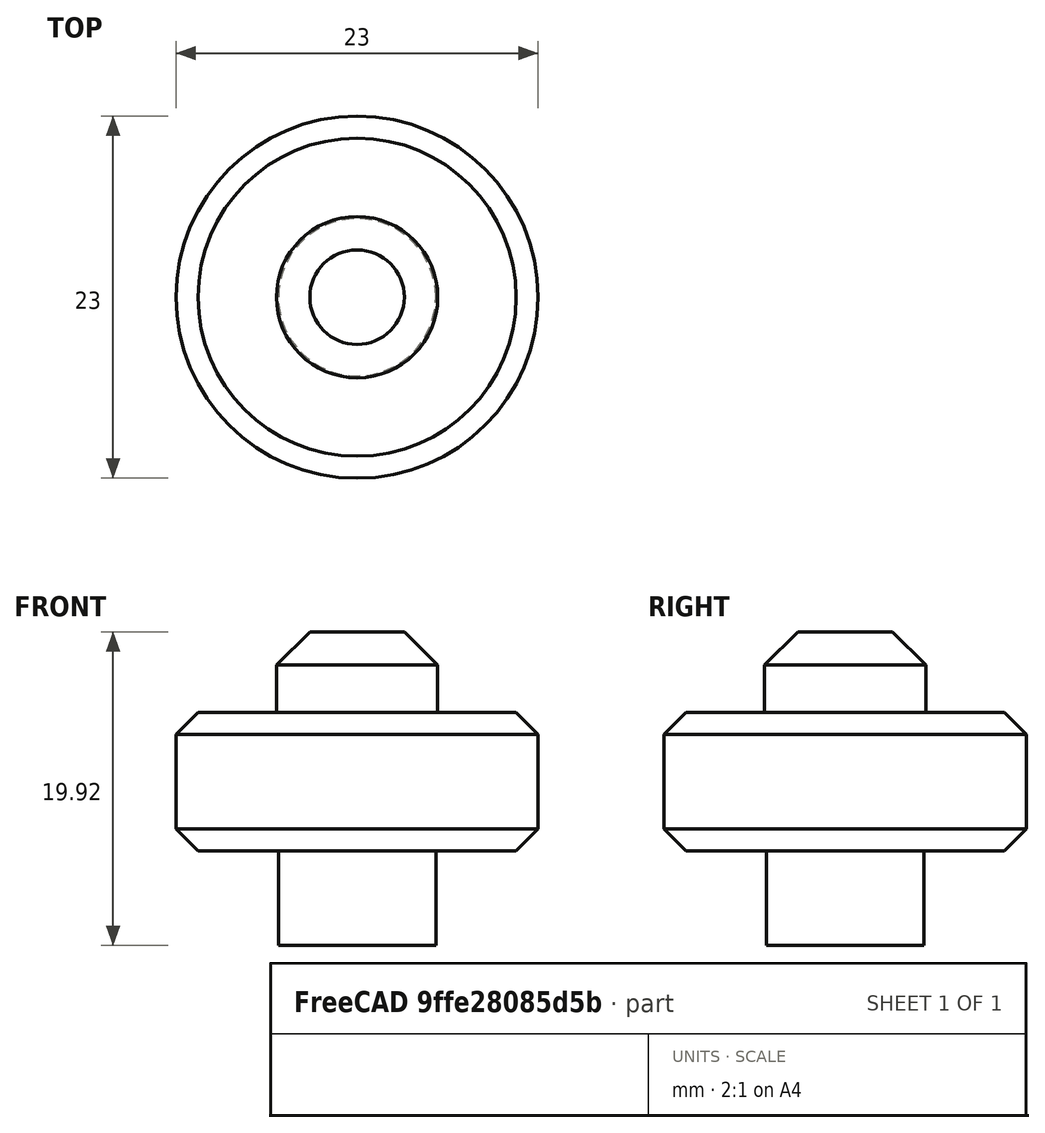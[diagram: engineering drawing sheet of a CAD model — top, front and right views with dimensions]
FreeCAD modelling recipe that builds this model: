
FCSTD DOCUMENT  (FreeCAD 0.20R29177 +426 (Git))
Label: GantryWheel
License: All rights reserved
LicenseURL: http://en.wikipedia.org/wiki/All_rights_reserved
objects: App::DocumentObjectGroup×3, PartDesign::CoordinateSystem×1, App::FeaturePython×1, Sketcher::SketchObject×1, PartDesign::Revolution×1, PartDesign::Body×1, App::Part×1
note: 5 computed .brp shape members not serialized (recipe doc carries the construction recipe); baked Part::Feature solids carry a one-line shape summary decoded from their .brp

FEATURE [App::DocumentObjectGroup] Parts
FEATURE [PartDesign::CoordinateSystem] LCS_Origin
  AttacherType = Attacher::AttachEngine3D
  MapMode = 2
  Support = -> [X_Axis]
FEATURE [App::FeaturePython] Variables  # WARN: FeaturePython — macro-defined, semantics opaque (R4)
  Type = App::PropertyContainer
FEATURE [App::DocumentObjectGroup] Constraints
FEATURE [App::DocumentObjectGroup] Configurations
FEATURE [Sketcher::SketchObject] Sketch
  FullyConstrained = true
  MapMode = 5
  Placement = pos=(0,0,0) rot=(1,0,0;1.5708rad)
  Support = -> [XZ_Plane001]
  sketch-geometry (11):
    g0: LineSegment StartX=0 StartY=19.9213 StartZ=0 EndX=3 EndY=19.9213 EndZ=0
    g1: LineSegment StartX=3 StartY=19.9213 StartZ=0 EndX=5.12132 EndY=17.8 EndZ=0
    g2: LineSegment StartX=5.12132 StartY=17.8 StartZ=0 EndX=5.12132 EndY=14.8 EndZ=0
    g3: LineSegment StartX=5.12132 StartY=14.8 StartZ=0 EndX=10.1 EndY=14.8 EndZ=0
    g4: LineSegment StartX=10.1 StartY=14.8 StartZ=0 EndX=11.5 EndY=13.4 EndZ=0
    g5: LineSegment StartX=11.5 StartY=13.4 StartZ=0 EndX=11.5 EndY=7.4 EndZ=0
    g6: LineSegment StartX=11.5 StartY=7.4 StartZ=0 EndX=10.1 EndY=6 EndZ=0
    g7: LineSegment StartX=10.1 StartY=6 StartZ=0 EndX=5 EndY=6 EndZ=0
    g8: LineSegment StartX=5 StartY=6 StartZ=0 EndX=5 EndY=0 EndZ=0
    g9: LineSegment StartX=5 StartY=0 StartZ=0 EndX=0 EndY=0 EndZ=0
    g10: LineSegment StartX=0 StartY=0 StartZ=0 EndX=0 EndY=19.9213 EndZ=0
  constraints (32):
    c: PointOnObject(g0,g-2)
    c: Horizontal(g0)
    c: Coincident(g0,g1)
    c: Coincident(g1,g2)
    c: Vertical(g2)
    c: Coincident(g2,g3)
    c: Horizontal(g3)
    c: Coincident(g3,g4)
    c: Coincident(g4,g5)
    c: Vertical(g5)
    c: Coincident(g5,g6)
    c: Coincident(g6,g7)
    c: Horizontal(g7)
    c: Coincident(g7,g8)
    c: Vertical(g8)
    c: PointOnObject(g9,g-1)
    c: Coincident(g9,g-1)
    c: Coincident(g9,g10)
    c: Coincident(g10,g0)
    c: Equal(g6,g4)
    c: DistanceY(g5,g5) = 6
    c: Angle(g6,g7) = 2.35619
    c: Angle(g3,g4) = 2.35619
    c: DistanceY(g6,g3) = 8.8
    c: Angle(g1,g2) = 2.35619
    c: Equal(g2,g1)
    c: Equal(g1,g0)
    c: DistanceX(g0,g0) = 3
    c: Coincident(g9,g8)
    c: DistanceY(g8,g8) = 6
    c: DistanceX(g9,g9) = 5
    c: DistanceX(g9,g5) = 11.5
FEATURE [PartDesign::Revolution] Revolution
  Angle = 360
  Axis = (0,-2e-16,1)
  Base = (0,0,0)
  Placement = pos=(0,0,0) rot=(1,0,0;1.5708rad)
  Profile = -> Sketch
  ReferenceAxis = -> Sketch [V_Axis]
  Reversed = true
FEATURE [PartDesign::Body] Body
  Group = -> [Sketch,Revolution]
  Origin = -> Origin001
  Tip = -> Revolution
FEATURE [App::Part] Assembly
  AssemblyType = Part::Link
  Group = -> [LCS_Origin,Variables,Constraints,Configurations,Body]
  Origin = -> Origin
  Type = Assembly
